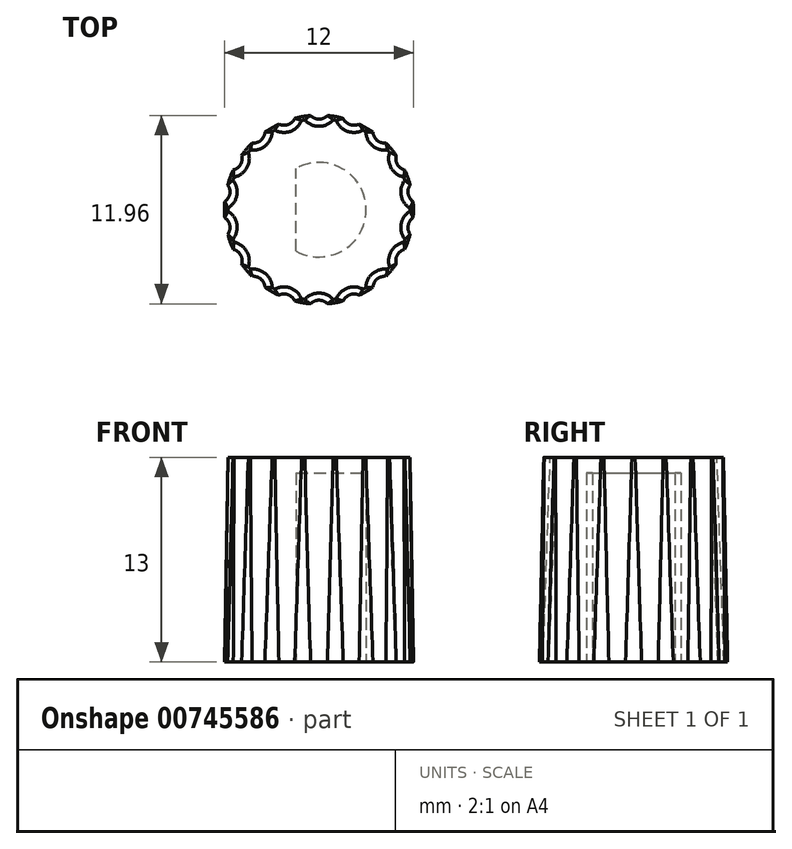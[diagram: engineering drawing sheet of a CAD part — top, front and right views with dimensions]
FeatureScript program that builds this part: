
annotation { "Feature Type Name" : "Feature", "Feature Type Description" : "" }
export const myFeature = defineFeature(function(context is Context, id is Id, definition is map)
    precondition{}
    {
        {
            var Q0;
            Q0=qCreatedBy(makeId("Top.planeOp"),FACE);
            var sketch = newSketch(context, id + "F0", { "sketchPlane" : qUnion([Q0])});
            skCircle(sketch, "E0", {"center": v(0, 0) * mm, "radius": 6 * mm});
            skSolve(sketch);
        }
        {
            var Q0;
            Q0=qCreatedBy(makeId("Top.planeOp"),FACE);
            var sketch = newSketch(context, id + "F1", { "sketchPlane" : qUnion([Q0])});
            skCircle(sketch, "E1", {"center": v(0, 0) * mm, "radius": 3 * mm});
            skLineSegment(sketch, "E2", {"start": v(3, 0) * mm, "end": v(3, 5.34) * mm});
            skLineSegment(sketch, "E3.top", {"start": v(3, 5.12) * mm, "end": v(-1.46, 5.12) * mm});
            skLineSegment(sketch, "E3.left", {"start": v(3, 0) * mm, "end": v(3, 5.12) * mm});
            skLineSegment(sketch, "E3.right", {"start": v(-1.46, 0) * mm, "end": v(-1.46, 5.12) * mm});
            skLineSegment(sketch, "E4.bottom", {"start": v(-1.46, 5.12) * mm, "end": v(3, 5.12) * mm});
            skLineSegment(sketch, "E4.top", {"start": v(-1.46, -5.04) * mm, "end": v(3, -5.04) * mm});
            skLineSegment(sketch, "E4.left", {"start": v(-1.46, 5.12) * mm, "end": v(-1.46, -5.04) * mm});
            skLineSegment(sketch, "E4.right", {"start": v(3, 5.12) * mm, "end": v(3, -5.04) * mm});
            skSolve(sketch);
        }
        {
            var Q0;
            Q0 = qSketchRegion(id + "F0", true);
            extrude(context, id + "F2", {"entities" : qUnion([Q0]), "depth" : 13 * mm, "offsetDistance" : 25 * mm, "hasDraft" : true, "draftAngle" : 1 * degree, "draftPullDirection" : true});
        }
        {
            var Q0;
            {var subQ2=sQuery(id+"F1.wireOp",EDGE,"E3.right");var subQ4=sQuery(id+"F1.wireOp",EDGE,"E4.left");var subQ5=makeQuery(id+"F1.imprint","INTERSECT",VERTEX,{"derivedFrom":[subQ2,subQ4]});Q0=makeQuery(id+"F1.imprint","IMPRINT",FACE,{"disambiguationData":[TD([[makeQuery(id+"F1.imprint","IMPRINT",EDGE,{"disambiguationData":[TD([[subQ5,-1.0]])],"derivedFrom":subQ2}),-1.0]])]});}
            extrude(context, id + "F3", {"entities" : qUnion([Q0]), "operationType" : NewBodyOperationType.REMOVE, "depth" : 12 * mm, "offsetDistance" : 25 * mm});
        }
        {
            var Q0;
            Q0=makeQuery(id+"F2.opExtrude","CAP_FACE",FACE,{"disambiguationData":[OSD([sQuery(id+"F0.wireOp",EDGE,"E0")])],"isStart":true});
            var sketch = newSketch(context, id + "F4", { "sketchPlane" : qUnion([Q0])});
            skArc(sketch, "E5.0", {"start": v(-2.46, -3.15) * mm, "mid": v(4, 0) * mm, "end": v(-2.46, 3.15) * mm});
            skLineSegment(sketch, "E5.1", {"start": v(-2.46, 3.15) * mm, "end": v(-2.46, -3.15) * mm});
            skCircle(sketch, "E6.0", {"center": v(0, 0) * mm, "radius": 5 * mm});
            skSolve(sketch);
        }
        {
            var Q0;
            Q0=makeQuery(id+"F4.imprint","IMPRINT",FACE,{"disambiguationData":[TD([[makeQuery(id+"F4.imprint","IMPRINT",EDGE,{"derivedFrom":sQuery(id+"F4.wireOp",EDGE,"E6.0")}),-1.0]])]});
            var sketch = newSketch(context, id + "F5", { "sketchPlane" : qUnion([Q0])});
            skCircle(sketch, "E7", {"center": v(0, 6.5) * mm, "radius": 0.75 * mm});
            skCircle(sketch, "E8.1.0", {"center": v(-2.22, 6.1) * mm, "radius": 0.75 * mm});
            skCircle(sketch, "E8.2.0", {"center": v(-4.18, 4.98) * mm, "radius": 0.75 * mm});
            skCircle(sketch, "E8.3.0", {"center": v(-5.63, 3.25) * mm, "radius": 0.75 * mm});
            skCircle(sketch, "E8.4.0", {"center": v(-6.4, 1.13) * mm, "radius": 0.75 * mm});
            skCircle(sketch, "E8.5.0", {"center": v(-6.4, -1.13) * mm, "radius": 0.75 * mm});
            skCircle(sketch, "E8.6.0", {"center": v(-5.63, -3.25) * mm, "radius": 0.75 * mm});
            skCircle(sketch, "E8.7.0", {"center": v(-4.18, -4.98) * mm, "radius": 0.75 * mm});
            skCircle(sketch, "E8.8.0", {"center": v(-2.22, -6.1) * mm, "radius": 0.75 * mm});
            skCircle(sketch, "E8.9.0", {"center": v(0, -6.5) * mm, "radius": 0.75 * mm});
            skCircle(sketch, "E8.10.0", {"center": v(2.22, -6.1) * mm, "radius": 0.75 * mm});
            skCircle(sketch, "E8.11.0", {"center": v(4.18, -4.98) * mm, "radius": 0.75 * mm});
            skCircle(sketch, "E8.12.0", {"center": v(5.63, -3.25) * mm, "radius": 0.75 * mm});
            skCircle(sketch, "E8.13.0", {"center": v(6.4, -1.13) * mm, "radius": 0.75 * mm});
            skCircle(sketch, "E8.14.0", {"center": v(6.4, 1.13) * mm, "radius": 0.75 * mm});
            skCircle(sketch, "E8.15.0", {"center": v(5.63, 3.25) * mm, "radius": 0.75 * mm});
            skCircle(sketch, "E8.16.0", {"center": v(4.18, 4.98) * mm, "radius": 0.75 * mm});
            skCircle(sketch, "E8.17.0", {"center": v(2.22, 6.1) * mm, "radius": 0.75 * mm});
            skPoint(sketch, "E8.center", {"position": v(0, 0) * mm});
            skSolve(sketch);
        }
        {
            var Q0;
            Q0 = qSketchRegion(id + "F5", true);
            extrude(context, id + "F6", {"entities" : qUnion([Q0]), "operationType" : NewBodyOperationType.REMOVE, "oppositeDirection" : true, "depth" : 13 * mm, "offsetDistance" : 25 * mm, "hasDraft" : true, "draftAngle" : 2 * degree});
        }
    });
